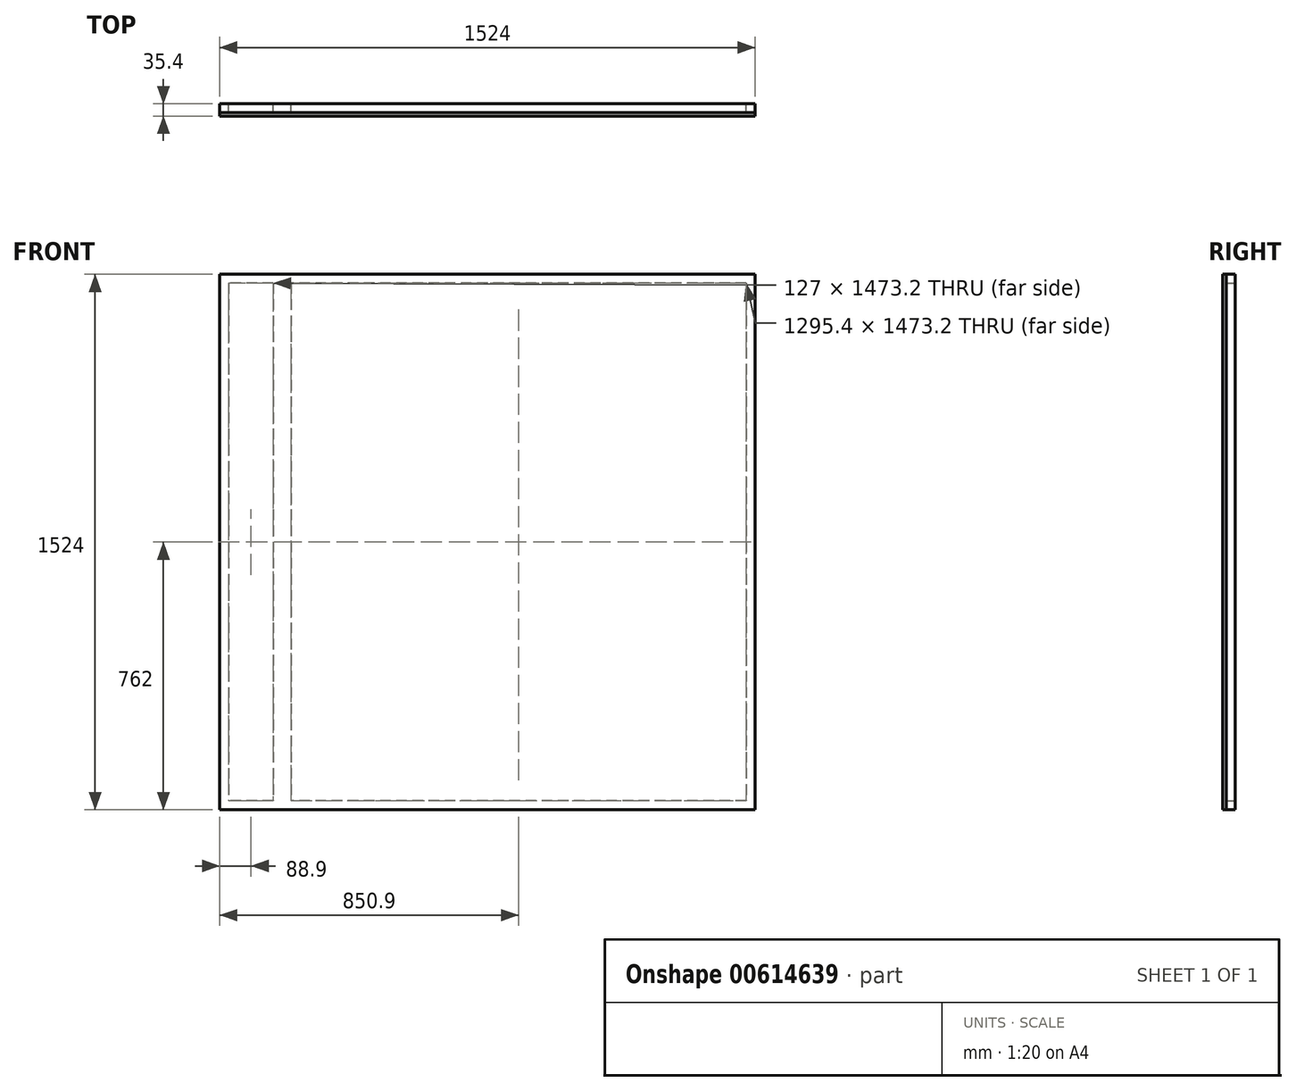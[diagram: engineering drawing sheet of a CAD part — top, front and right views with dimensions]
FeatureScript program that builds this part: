
annotation { "Feature Type Name" : "Feature", "Feature Type Description" : "" }
export const myFeature = defineFeature(function(context is Context, id is Id, definition is map)
    precondition{}
    {
        {
            var Q0;
            Q0=qCreatedBy(makeId("Front.planeOp"),FACE);
            var sketch = newSketch(context, id + "F0", { "sketchPlane" : qUnion([Q0])});
            skLineSegment(sketch, "E0.bottom", {"start": v(762, -762) * mm, "end": v(-762, -762) * mm});
            skLineSegment(sketch, "E0.top", {"start": v(762, 762) * mm, "end": v(-762, 762) * mm});
            skLineSegment(sketch, "E0.left", {"start": v(762, -762) * mm, "end": v(762, 762) * mm});
            skLineSegment(sketch, "E0.right", {"start": v(-762, -762) * mm, "end": v(-762, 762) * mm});
            skPoint(sketch, "E0.middle", {"position": v(0, 0) * mm});
            skSolve(sketch);
        }
        {
            var Q0;
            Q0=makeQuery(id+"F0.imprint","IMPRINT",FACE,{"disambiguationData":[TD([[makeQuery(id+"F0.imprint","IMPRINT",EDGE,{"derivedFrom":sQuery(id+"F0.wireOp",EDGE,"E0.bottom")}),-1.0]])]});
            extrude(context, id + "F1", {"entities" : qUnion([Q0]), "depth" : 10 * mm});
        }
        {
            var Q0;
            Q0=makeQuery(id+"F1.opExtrude","CAP_FACE",FACE,{"disambiguationData":[OSD([sQuery(id+"F0.wireOp",EDGE,"E0.bottom"),sQuery(id+"F0.wireOp",EDGE,"E0.top"),sQuery(id+"F0.wireOp",EDGE,"E0.left"),sQuery(id+"F0.wireOp",EDGE,"E0.right")])],"isStart":true});
            var sketch = newSketch(context, id + "F2", { "sketchPlane" : qUnion([Q0])});
            skLineSegment(sketch, "E1.bottom", {"start": v(-762, 762) * mm, "end": v(762, 762) * mm});
            skLineSegment(sketch, "E1.top", {"start": v(-762, -762) * mm, "end": v(762, -762) * mm});
            skLineSegment(sketch, "E1.left", {"start": v(-762, 762) * mm, "end": v(-762, -762) * mm});
            skLineSegment(sketch, "E1.right", {"start": v(762, 762) * mm, "end": v(762, -762) * mm});
            skSolve(sketch);
        }
        {
            var Q0;
            Q0=makeQuery(id+"F2.imprint","IMPRINT",FACE,{"disambiguationData":[TD([[makeQuery(id+"F2.imprint","IMPRINT",EDGE,{"derivedFrom":sQuery(id+"F2.wireOp",EDGE,"E1.bottom")}),-1.0]])]});
            extrude(context, id + "F3", {"entities" : qUnion([Q0]), "depth" : 25.4 * mm, "offsetDistance" : 25.4 * mm});
        }
        {
            var Q0;
            Q0=makeQuery(id+"F3.opExtrude","CAP_FACE",FACE,{"disambiguationData":[OSD([sQuery(id+"F2.wireOp",EDGE,"E1.bottom"),sQuery(id+"F2.wireOp",EDGE,"E1.top"),sQuery(id+"F2.wireOp",EDGE,"E1.left"),sQuery(id+"F2.wireOp",EDGE,"E1.right")])],"isStart":false});
            var sketch = newSketch(context, id + "F4", { "sketchPlane" : qUnion([Q0])});
            skLineSegment(sketch, "E2.bottom", {"start": v(-736.6, 736.6) * mm, "end": v(558.8, 736.6) * mm});
            skLineSegment(sketch, "E2.top", {"start": v(-736.6, -736.6) * mm, "end": v(558.8, -736.6) * mm});
            skLineSegment(sketch, "E2.left", {"start": v(-736.6, 736.6) * mm, "end": v(-736.6, -736.6) * mm});
            skLineSegment(sketch, "E2.right", {"start": v(558.8, 736.6) * mm, "end": v(558.8, -736.6) * mm});
            skLineSegment(sketch, "E3.bottom", {"start": v(-609.6, 736.6) * mm, "end": v(609.6, 736.6) * mm});
            skLineSegment(sketch, "E3.top", {"start": v(-609.6, -736.6) * mm, "end": v(609.6, -736.6) * mm});
            skLineSegment(sketch, "E3.left", {"start": v(609.6, 736.6) * mm, "end": v(609.6, -736.6) * mm});
            skLineSegment(sketch, "E3.right", {"start": v(-609.6, 736.6) * mm, "end": v(-609.6, -736.6) * mm});
            skLineSegment(sketch, "E4.bottom", {"start": v(-558.8, 736.6) * mm, "end": v(736.6, 736.6) * mm});
            skLineSegment(sketch, "E4.top", {"start": v(-558.8, -736.6) * mm, "end": v(736.6, -736.6) * mm});
            skLineSegment(sketch, "E4.left", {"start": v(-558.8, 736.6) * mm, "end": v(-558.8, -736.6) * mm});
            skLineSegment(sketch, "E4.right", {"start": v(736.6, 736.6) * mm, "end": v(736.6, -736.6) * mm});
            skSolve(sketch);
        }
        {
            var Q0;
            Q0=makeQuery(id+"F4.imprint","IMPRINT",FACE,{"disambiguationData":[TD([[makeQuery(id+"F4.imprint","IMPRINT",EDGE,{"derivedFrom":sQuery(id+"F4.wireOp",EDGE,"E2.bottom")}),-1.0]])]});
            var Q1;
            {var subQ0=sQuery(id+"F4.wireOp",EDGE,"E2.right");Q1=makeQuery(id+"F4.imprint","IMPRINT",FACE,{"disambiguationData":[TD([[makeQuery(id+"F4.imprint","IMPRINT",EDGE,{"derivedFrom":subQ0}),-1.0]])]});}
            var Q2;
            {var subQ0=sQuery(id+"F4.wireOp",EDGE,"E3.left");Q2=makeQuery(id+"F4.imprint","IMPRINT",FACE,{"disambiguationData":[TD([[makeQuery(id+"F4.imprint","IMPRINT",EDGE,{"derivedFrom":subQ0}),1.0]])]});}
            extrude(context, id + "F5", {"entities" : qUnion([Q0, Q1, Q2]), "operationType" : NewBodyOperationType.REMOVE, "oppositeDirection" : true, "depth" : 25.4 * mm, "offsetDistance" : 25.4 * mm});
        }
    });
